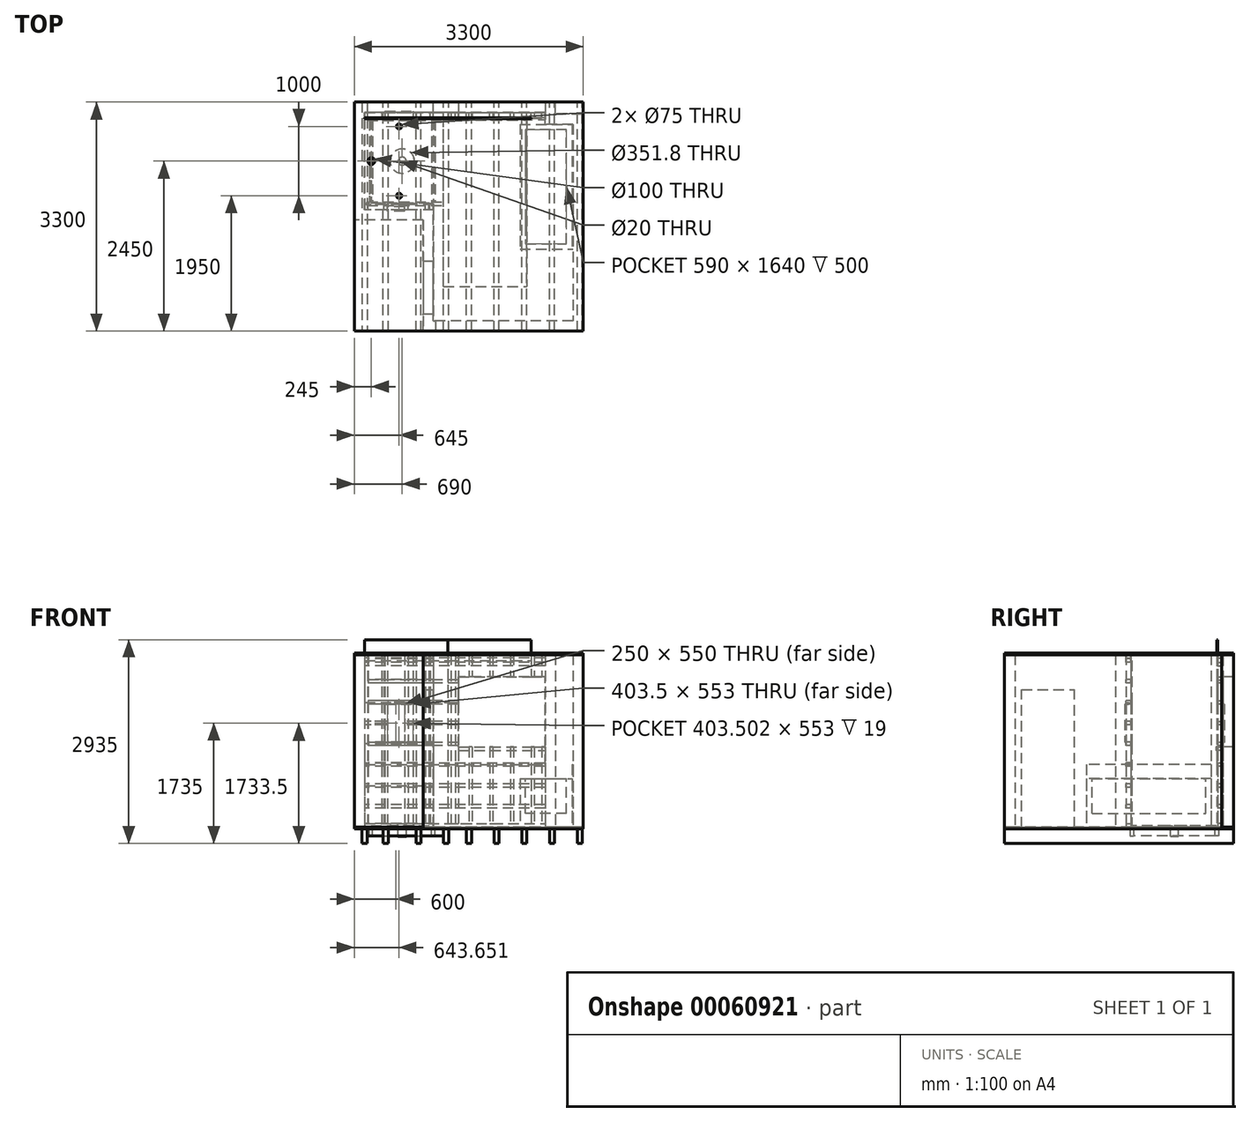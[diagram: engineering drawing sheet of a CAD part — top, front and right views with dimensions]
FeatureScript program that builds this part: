
annotation { "Feature Type Name" : "Feature", "Feature Type Description" : "" }
export const myFeature = defineFeature(function(context is Context, id is Id, definition is map)
    precondition{}
    {
        {
            var Q0;
            Q0=qCreatedBy(makeId("Top.planeOp"),FACE);
            var sketch = newSketch(context, id + "F0", { "sketchPlane" : qUnion([Q0])});
            skLineSegment(sketch, "E0.bottom", {"start": v(1500, -1500) * mm, "end": v(-510, -1500) * mm});
            skLineSegment(sketch, "E0.top", {"start": v(1100, 1500) * mm, "end": v(-1500, 1500) * mm});
            skLineSegment(sketch, "E0.left", {"start": v(1500, -1500) * mm, "end": v(1500, 1331.1) * mm});
            skLineSegment(sketch, "E0.right", {"start": v(-1500, 100) * mm, "end": v(-1500, 1500) * mm});
            skPoint(sketch, "E0.middle", {"position": v(0, 0) * mm});
            skLineSegment(sketch, "E1", {"start": v(-1500, 100) * mm, "end": v(-510, 100) * mm});
            skLineSegment(sketch, "E2", {"start": v(-510, 100) * mm, "end": v(-510, -1500) * mm});
            skLineSegment(sketch, "E3", {"start": v(1100, 1500) * mm, "end": v(1100, 1331.1) * mm});
            skLineSegment(sketch, "E4", {"start": v(1100, 1331.1) * mm, "end": v(1500, 1331.1) * mm});
            skLineSegment(sketch, "E5.0", {"start": v(1650, -1650) * mm, "end": v(1650, 1481.1) * mm});
            skLineSegment(sketch, "E5.1", {"start": v(1250, 1481.1) * mm, "end": v(1650, 1481.1) * mm});
            skLineSegment(sketch, "E5.2", {"start": v(1650, -1650) * mm, "end": v(-660, -1650) * mm});
            skLineSegment(sketch, "E5.3", {"start": v(1250, 1650) * mm, "end": v(1250, 1481.1) * mm});
            skLineSegment(sketch, "E5.4", {"start": v(-660, -50) * mm, "end": v(-660, -1650) * mm});
            skLineSegment(sketch, "E5.5", {"start": v(-1650, -50) * mm, "end": v(-660, -50) * mm});
            skLineSegment(sketch, "E5.6", {"start": v(-1650, -50) * mm, "end": v(-1650, 1650) * mm});
            skLineSegment(sketch, "E5.7", {"start": v(1250, 1650) * mm, "end": v(-1650, 1650) * mm});
            skSolve(sketch);
        }
        {
            var Q0;
            Q0=makeQuery(id+"F0.imprint","IMPRINT",FACE,{"disambiguationData":[TD([[makeQuery(id+"F0.imprint","IMPRINT",EDGE,{"derivedFrom":sQuery(id+"F0.wireOp",EDGE,"E0.bottom")}),1.0]])]});
            extrude(context, id + "F1", {"entities" : qUnion([Q0]), "depth" : 2510 * mm});
        }
        {
            var Q0;
            Q0=makeQuery(id+"F1.opExtrude","CAP_FACE",FACE,{"disambiguationData":[OSD([sQuery(id+"F0.wireOp",EDGE,"E0.bottom"),sQuery(id+"F0.wireOp",EDGE,"E0.top"),sQuery(id+"F0.wireOp",EDGE,"E0.left"),sQuery(id+"F0.wireOp",EDGE,"E0.right"),sQuery(id+"F0.wireOp",EDGE,"E1"),sQuery(id+"F0.wireOp",EDGE,"E2"),sQuery(id+"F0.wireOp",EDGE,"E3"),sQuery(id+"F0.wireOp",EDGE,"E4"),sQuery(id+"F0.wireOp",EDGE,"E5.0"),sQuery(id+"F0.wireOp",EDGE,"E5.1"),sQuery(id+"F0.wireOp",EDGE,"E5.2"),sQuery(id+"F0.wireOp",EDGE,"E5.3"),sQuery(id+"F0.wireOp",EDGE,"E5.4"),sQuery(id+"F0.wireOp",EDGE,"E5.5"),sQuery(id+"F0.wireOp",EDGE,"E5.6"),sQuery(id+"F0.wireOp",EDGE,"E5.7")])],"isStart":true});
            var sketch = newSketch(context, id + "F2", { "sketchPlane" : qUnion([Q0])});
            skLineSegment(sketch, "E6.bottom", {"start": v(1650, 1650) * mm, "end": v(-1650, 1650) * mm});
            skLineSegment(sketch, "E6.top", {"start": v(1650, -1650) * mm, "end": v(-1650, -1650) * mm});
            skLineSegment(sketch, "E6.left", {"start": v(1650, 1650) * mm, "end": v(1650, -1650) * mm});
            skLineSegment(sketch, "E6.right", {"start": v(-1650, 1650) * mm, "end": v(-1650, -1650) * mm});
            skSolve(sketch);
        }
        {
            var Q0;
            Q0 = qSketchRegion(id + "F2", true);
            extrude(context, id + "F3", {"entities" : qUnion([Q0]), "operationType" : NewBodyOperationType.ADD, "oppositeDirection" : true, "depth" : 25 * mm});
        }
        {
            var Q0;
            Q0=makeQuery(id+"F1.opExtrude","SWEPT_FACE",FACE,{"disambiguationData":[OSD([sQuery(id+"F0.wireOp",EDGE,"E2")])]});
            var sketch = newSketch(context, id + "F4", { "sketchPlane" : qUnion([Q0])});
            skLineSegment(sketch, "E7.bottom", {"start": v(-1402.14, 25) * mm, "end": v(-640.14, 25) * mm});
            skLineSegment(sketch, "E7.top", {"start": v(-1402.14, 2006) * mm, "end": v(-640.14, 2006) * mm});
            skLineSegment(sketch, "E7.left", {"start": v(-1402.14, 25) * mm, "end": v(-1402.14, 2006) * mm});
            skLineSegment(sketch, "E7.right", {"start": v(-640.14, 25) * mm, "end": v(-640.14, 2006) * mm});
            skSolve(sketch);
        }
        {
            var Q0;
            Q0 = qSketchRegion(id + "F4", true);
            extrude(context, id + "F5", {"entities" : qUnion([Q0]), "operationType" : NewBodyOperationType.REMOVE, "endBound" : BoundingType.UP_TO_NEXT, "oppositeDirection" : true, "depth" : 25 * mm});
        }
        {
            var Q0;
            Q0=makeQuery(id+"F1.opExtrude","SWEPT_FACE",FACE,{"disambiguationData":[OSD([sQuery(id+"F0.wireOp",EDGE,"E0.top")])]});
            var sketch = newSketch(context, id + "F6", { "sketchPlane" : qUnion([Q0])});
            skLineSegment(sketch, "E8.bottom", {"start": v(-150, 2190) * mm, "end": v(1100, 2190) * mm});
            skLineSegment(sketch, "E8.top", {"start": v(-150, 1180) * mm, "end": v(1100, 1180) * mm});
            skLineSegment(sketch, "E8.left", {"start": v(-150, 2190) * mm, "end": v(-150, 1180) * mm});
            skLineSegment(sketch, "E8.right", {"start": v(1100, 2190) * mm, "end": v(1100, 1180) * mm});
            skSolve(sketch);
        }
        {
            var Q0;
            Q0 = qSketchRegion(id + "F6", true);
            extrude(context, id + "F7", {"entities" : qUnion([Q0]), "operationType" : NewBodyOperationType.REMOVE, "endBound" : BoundingType.UP_TO_NEXT, "oppositeDirection" : true, "depth" : 25 * mm, "hasSecondDirection" : true, "secondDirectionBound" : BoundingType.UP_TO_NEXT, "secondDirectionOppositeDirection" : false, "secondDirectionDepth" : 25 * mm});
        }
        {
            var Q0;
            {var subQ0=sQuery(id+"F2.wireOp",EDGE,"E6.right");var subQ1=sQuery(id+"F2.wireOp",EDGE,"E6.bottom");var subQ2=makeQuery(id+"F3.opExtrude","CAP_FACE",FACE,{"disambiguationData":[OSD([subQ1,sQuery(id+"F2.wireOp",EDGE,"E6.top"),sQuery(id+"F2.wireOp",EDGE,"E6.left"),subQ0])],"isStart":false});Q0=makeQuery(id+"F5.boolean.opBoolean","MERGE",FACE,{"derivedFrom":[makeQuery(id+"F3.boolean.opBoolean","SPLIT",FACE,{"disambiguationData":[TD([makeQuery(id+"F1.opExtrude","SWEPT_FACE",FACE,{"disambiguationData":[OSD([sQuery(id+"F0.wireOp",EDGE,"E5.2")])]})])],"derivedFrom":subQ2}),makeQuery(id+"F3.boolean.opBoolean","SPLIT",FACE,{"disambiguationData":[TD([makeQuery(id+"F1.opExtrude","SWEPT_FACE",FACE,{"disambiguationData":[OSD([sQuery(id+"F0.wireOp",EDGE,"E0.bottom")])]})])],"derivedFrom":subQ2}),makeQuery(id+"F5.opExtrude","SWEPT_FACE",FACE,{"disambiguationData":[OSD([sQuery(id+"F4.wireOp",EDGE,"E7.bottom")])]})]});}
            var sketch = newSketch(context, id + "F8", { "sketchPlane" : qUnion([Q0])});
            skLineSegment(sketch, "E9.bottom", {"start": v(-1500, 1500) * mm, "end": v(1100, 1500) * mm});
            skLineSegment(sketch, "E9.top", {"start": v(-1500, 1425) * mm, "end": v(1100, 1425) * mm});
            skLineSegment(sketch, "E9.left", {"start": v(-1500, 1500) * mm, "end": v(-1500, 1425) * mm});
            skLineSegment(sketch, "E9.right", {"start": v(1100, 1500) * mm, "end": v(1100, 1425) * mm});
            skSolve(sketch);
        }
        {
            var Q0;
            Q0 = qSketchRegion(id + "F8", true);
            extrude(context, id + "F9", {"entities" : qUnion([Q0]), "depth" : 50 * mm});
        }
        {
            var Q0;
            Q0=makeQuery(id+"F9.opExtrude","CAP_FACE",FACE,{"disambiguationData":[OSD([sQuery(id+"F8.wireOp",EDGE,"E9.bottom"),sQuery(id+"F8.wireOp",EDGE,"E9.top"),sQuery(id+"F8.wireOp",EDGE,"E9.left"),sQuery(id+"F8.wireOp",EDGE,"E9.right")])],"isStart":false});
            var sketch = newSketch(context, id + "F10", { "sketchPlane" : qUnion([Q0])});
            skLineSegment(sketch, "E10.bottom", {"start": v(-1500, 1425) * mm, "end": v(-1455, 1425) * mm});
            skLineSegment(sketch, "E10.top", {"start": v(-1500, 1500) * mm, "end": v(-1455, 1500) * mm});
            skLineSegment(sketch, "E10.left", {"start": v(-1500, 1425) * mm, "end": v(-1500, 1500) * mm});
            skLineSegment(sketch, "E10.right", {"start": v(-1455, 1425) * mm, "end": v(-1455, 1500) * mm});
            skLineSegment(sketch, "E11.bottom", {"start": v(1100, 1500) * mm, "end": v(1050, 1500) * mm});
            skLineSegment(sketch, "E11.top", {"start": v(1100, 1425) * mm, "end": v(1050, 1425) * mm});
            skLineSegment(sketch, "E11.left", {"start": v(1100, 1500) * mm, "end": v(1100, 1425) * mm});
            skLineSegment(sketch, "E11.right", {"start": v(1050, 1500) * mm, "end": v(1050, 1425) * mm});
            skLineSegment(sketch, "E12.bottom", {"start": v(900, 1500) * mm, "end": v(945, 1500) * mm});
            skLineSegment(sketch, "E12.top", {"start": v(900, 1425) * mm, "end": v(945, 1425) * mm});
            skLineSegment(sketch, "E12.left", {"start": v(900, 1500) * mm, "end": v(900, 1425) * mm});
            skLineSegment(sketch, "E12.right", {"start": v(945, 1500) * mm, "end": v(945, 1425) * mm});
            skLineSegment(sketch, "E13.bottom", {"start": v(600, 1500) * mm, "end": v(645, 1500) * mm});
            skLineSegment(sketch, "E13.top", {"start": v(600, 1425) * mm, "end": v(645, 1425) * mm});
            skLineSegment(sketch, "E13.left", {"start": v(600, 1500) * mm, "end": v(600, 1425) * mm});
            skLineSegment(sketch, "E13.right", {"start": v(645, 1500) * mm, "end": v(645, 1425) * mm});
            skLineSegment(sketch, "E14.bottom", {"start": v(300, 1500) * mm, "end": v(345, 1500) * mm});
            skLineSegment(sketch, "E14.top", {"start": v(300, 1425) * mm, "end": v(345, 1425) * mm});
            skLineSegment(sketch, "E14.left", {"start": v(300, 1500) * mm, "end": v(300, 1425) * mm});
            skLineSegment(sketch, "E14.right", {"start": v(345, 1500) * mm, "end": v(345, 1425) * mm});
            skLineSegment(sketch, "E15.bottom", {"start": v(0, 1500) * mm, "end": v(45, 1500) * mm});
            skLineSegment(sketch, "E15.top", {"start": v(0, 1425) * mm, "end": v(45, 1425) * mm});
            skLineSegment(sketch, "E15.left", {"start": v(0, 1500) * mm, "end": v(0, 1425) * mm});
            skLineSegment(sketch, "E15.right", {"start": v(45, 1500) * mm, "end": v(45, 1425) * mm});
            skLineSegment(sketch, "E16.bottom", {"start": v(-300, 1500) * mm, "end": v(-255, 1500) * mm});
            skLineSegment(sketch, "E16.top", {"start": v(-300, 1425) * mm, "end": v(-255, 1425) * mm});
            skLineSegment(sketch, "E16.left", {"start": v(-300, 1500) * mm, "end": v(-300, 1425) * mm});
            skLineSegment(sketch, "E16.right", {"start": v(-255, 1500) * mm, "end": v(-255, 1425) * mm});
            skLineSegment(sketch, "E17.bottom", {"start": v(-804.6, 1500) * mm, "end": v(-757.44, 1500) * mm});
            skLineSegment(sketch, "E17.top", {"start": v(-804.6, 1425) * mm, "end": v(-757.44, 1425) * mm});
            skLineSegment(sketch, "E17.left", {"start": v(-804.6, 1500) * mm, "end": v(-804.6, 1425) * mm});
            skLineSegment(sketch, "E17.right", {"start": v(-757.44, 1500) * mm, "end": v(-757.44, 1425) * mm});
            skLineSegment(sketch, "E18.bottom", {"start": v(-1255.25, 1500) * mm, "end": v(-1208.1, 1500) * mm});
            skLineSegment(sketch, "E18.top", {"start": v(-1255.25, 1425) * mm, "end": v(-1208.1, 1425) * mm});
            skLineSegment(sketch, "E18.left", {"start": v(-1255.25, 1500) * mm, "end": v(-1255.25, 1425) * mm});
            skLineSegment(sketch, "E18.right", {"start": v(-1208.1, 1500) * mm, "end": v(-1208.1, 1425) * mm});
            skLineSegment(sketch, "E19.bottom", {"start": v(-195, 1425) * mm, "end": v(-150, 1425) * mm});
            skLineSegment(sketch, "E19.top", {"start": v(-195, 1500) * mm, "end": v(-150, 1500) * mm});
            skLineSegment(sketch, "E19.left", {"start": v(-195, 1425) * mm, "end": v(-195, 1500) * mm});
            skLineSegment(sketch, "E19.right", {"start": v(-150, 1425) * mm, "end": v(-150, 1500) * mm});
            skLineSegment(sketch, "E20.bottom", {"start": v(-555, 1425) * mm, "end": v(-510, 1425) * mm});
            skLineSegment(sketch, "E20.top", {"start": v(-555, 1500) * mm, "end": v(-510, 1500) * mm});
            skLineSegment(sketch, "E20.left", {"start": v(-555, 1425) * mm, "end": v(-555, 1500) * mm});
            skLineSegment(sketch, "E20.right", {"start": v(-510, 1425) * mm, "end": v(-510, 1500) * mm});
            skSolve(sketch);
        }
        {
            var Q0;
            Q0 = qSketchRegion(id + "F10", true);
            var Q1;
            Q1=makeQuery(id+"F1.opExtrude","CAP_FACE",FACE,{"disambiguationData":[OSD([sQuery(id+"F0.wireOp",EDGE,"E0.bottom"),sQuery(id+"F0.wireOp",EDGE,"E0.top"),sQuery(id+"F0.wireOp",EDGE,"E0.left"),sQuery(id+"F0.wireOp",EDGE,"E0.right"),sQuery(id+"F0.wireOp",EDGE,"E1"),sQuery(id+"F0.wireOp",EDGE,"E2"),sQuery(id+"F0.wireOp",EDGE,"E3"),sQuery(id+"F0.wireOp",EDGE,"E4"),sQuery(id+"F0.wireOp",EDGE,"E5.0"),sQuery(id+"F0.wireOp",EDGE,"E5.1"),sQuery(id+"F0.wireOp",EDGE,"E5.2"),sQuery(id+"F0.wireOp",EDGE,"E5.3"),sQuery(id+"F0.wireOp",EDGE,"E5.4"),sQuery(id+"F0.wireOp",EDGE,"E5.5"),sQuery(id+"F0.wireOp",EDGE,"E5.6"),sQuery(id+"F0.wireOp",EDGE,"E5.7")])],"isStart":false});
            extrude(context, id + "F11", {"entities" : qUnion([Q0]), "endBound" : BoundingType.UP_TO_SURFACE, "endBoundEntityFace" : qUnion([Q1]), "depth" : 25 * mm});
        }
        {
            var Q0;
            Q0=makeQuery(id+"F1.opExtrude","SWEPT_FACE",FACE,{"disambiguationData":[OSD([sQuery(id+"F0.wireOp",EDGE,"E0.right")])]});
            var sketch = newSketch(context, id + "F12", { "sketchPlane" : qUnion([Q0])});
            skLineSegment(sketch, "E21.bottom", {"start": v(1425, 2510) * mm, "end": v(1500, 2510) * mm});
            skLineSegment(sketch, "E21.top", {"start": v(1425, 2463) * mm, "end": v(1500, 2463) * mm});
            skLineSegment(sketch, "E21.left", {"start": v(1425, 2510) * mm, "end": v(1425, 2463) * mm});
            skLineSegment(sketch, "E21.right", {"start": v(1500, 2510) * mm, "end": v(1500, 2463) * mm});
            skLineSegment(sketch, "E22.bottom", {"start": v(1500, 2147) * mm, "end": v(1425, 2147) * mm});
            skLineSegment(sketch, "E22.top", {"start": v(1500, 2100) * mm, "end": v(1425, 2100) * mm});
            skLineSegment(sketch, "E22.left", {"start": v(1500, 2147) * mm, "end": v(1500, 2100) * mm});
            skLineSegment(sketch, "E22.right", {"start": v(1425, 2147) * mm, "end": v(1425, 2100) * mm});
            skLineSegment(sketch, "E23.bottom", {"start": v(1500, 1847) * mm, "end": v(1425, 1847) * mm});
            skLineSegment(sketch, "E23.top", {"start": v(1500, 1800) * mm, "end": v(1425, 1800) * mm});
            skLineSegment(sketch, "E23.left", {"start": v(1500, 1847) * mm, "end": v(1500, 1800) * mm});
            skLineSegment(sketch, "E23.right", {"start": v(1425, 1847) * mm, "end": v(1425, 1800) * mm});
            skLineSegment(sketch, "E24.bottom", {"start": v(1500, 1547) * mm, "end": v(1425, 1547) * mm});
            skLineSegment(sketch, "E24.top", {"start": v(1500, 1500) * mm, "end": v(1425, 1500) * mm});
            skLineSegment(sketch, "E24.left", {"start": v(1500, 1547) * mm, "end": v(1500, 1500) * mm});
            skLineSegment(sketch, "E24.right", {"start": v(1425, 1547) * mm, "end": v(1425, 1500) * mm});
            skLineSegment(sketch, "E25.bottom", {"start": v(1500, 1247) * mm, "end": v(1425, 1247) * mm});
            skLineSegment(sketch, "E25.top", {"start": v(1500, 1200) * mm, "end": v(1425, 1200) * mm});
            skLineSegment(sketch, "E25.left", {"start": v(1500, 1247) * mm, "end": v(1500, 1200) * mm});
            skLineSegment(sketch, "E25.right", {"start": v(1425, 1247) * mm, "end": v(1425, 1200) * mm});
            skLineSegment(sketch, "E26.bottom", {"start": v(1500, 947) * mm, "end": v(1425, 947) * mm});
            skLineSegment(sketch, "E26.top", {"start": v(1500, 900) * mm, "end": v(1425, 900) * mm});
            skLineSegment(sketch, "E26.left", {"start": v(1500, 947) * mm, "end": v(1500, 900) * mm});
            skLineSegment(sketch, "E26.right", {"start": v(1425, 947) * mm, "end": v(1425, 900) * mm});
            skLineSegment(sketch, "E27.bottom", {"start": v(1500, 647) * mm, "end": v(1425, 647) * mm});
            skLineSegment(sketch, "E27.top", {"start": v(1500, 600) * mm, "end": v(1425, 600) * mm});
            skLineSegment(sketch, "E27.left", {"start": v(1500, 647) * mm, "end": v(1500, 600) * mm});
            skLineSegment(sketch, "E27.right", {"start": v(1425, 647) * mm, "end": v(1425, 600) * mm});
            skLineSegment(sketch, "E28.bottom", {"start": v(1500, 347) * mm, "end": v(1425, 347) * mm});
            skLineSegment(sketch, "E28.top", {"start": v(1500, 300) * mm, "end": v(1425, 300) * mm});
            skLineSegment(sketch, "E28.left", {"start": v(1500, 347) * mm, "end": v(1500, 300) * mm});
            skLineSegment(sketch, "E28.right", {"start": v(1425, 347) * mm, "end": v(1425, 300) * mm});
            skLineSegment(sketch, "E29.bottom", {"start": v(1425, 2400) * mm, "end": v(1500, 2400) * mm});
            skLineSegment(sketch, "E29.top", {"start": v(1425, 2353) * mm, "end": v(1500, 2353) * mm});
            skLineSegment(sketch, "E29.left", {"start": v(1425, 2400) * mm, "end": v(1425, 2353) * mm});
            skLineSegment(sketch, "E29.right", {"start": v(1500, 2400) * mm, "end": v(1500, 2353) * mm});
            skSolve(sketch);
        }
        {
            var Q0;
            Q0 = qSketchRegion(id + "F12", true);
            var Q1;
            Q1=makeQuery(id+"F7.boolean.opBoolean","MERGE",FACE,{"derivedFrom":[makeQuery(id+"F1.opExtrude","SWEPT_FACE",FACE,{"disambiguationData":[OSD([sQuery(id+"F0.wireOp",EDGE,"E3")])]}),makeQuery(id+"F7.opExtrude","SWEPT_FACE",FACE,{"disambiguationData":[OSD([sQuery(id+"F6.wireOp",EDGE,"E8.right")])]})]});
            extrude(context, id + "F13", {"entities" : qUnion([Q0]), "endBound" : BoundingType.UP_TO_SURFACE, "endBoundEntityFace" : qUnion([Q1]), "depth" : 25 * mm});
        }
        {
            var Q0;
            Q0=makeQuery(id+"F11.opExtrude","SWEPT_FACE",FACE,{"disambiguationData":[OSD([sQuery(id+"F10.wireOp",EDGE,"E17.top")])]});
            var sketch = newSketch(context, id + "F14", { "sketchPlane" : qUnion([Q0])});
            skLineSegment(sketch, "E30.bottom", {"start": v(-1500, 925) * mm, "end": v(-300, 925) * mm});
            skLineSegment(sketch, "E30.top", {"start": v(-1500, 25) * mm, "end": v(-300, 25) * mm});
            skLineSegment(sketch, "E30.left", {"start": v(-1500, 925) * mm, "end": v(-1500, 25) * mm});
            skLineSegment(sketch, "E30.right", {"start": v(-300, 925) * mm, "end": v(-300, 25) * mm});
            skSolve(sketch);
        }
        {
            var Q0;
            Q0 = qSketchRegion(id + "F14", true);
            extrude(context, id + "F15", {"entities" : qUnion([Q0]), "depth" : 12 * mm});
        }
        {
            var Q0;
            Q0=makeQuery(id+"F15.opExtrude","SWEPT_BODY",BODY,{"disambiguationData":[OSD([sQuery(id+"F14.wireOp",EDGE,"E30.bottom"),sQuery(id+"F14.wireOp",EDGE,"E30.top"),sQuery(id+"F14.wireOp",EDGE,"E30.left"),sQuery(id+"F14.wireOp",EDGE,"E30.right")])]});
            transform(context, id + "F16", {"entities" : qUnion([Q0]), "transformType" : TransformType.COPY});
        }
        {
            var Q0;
            Q0=makeQuery(id+"F15.opExtrude","SWEPT_BODY",BODY,{"disambiguationData":[OSD([sQuery(id+"F14.wireOp",EDGE,"E30.bottom"),sQuery(id+"F14.wireOp",EDGE,"E30.top"),sQuery(id+"F14.wireOp",EDGE,"E30.left"),sQuery(id+"F14.wireOp",EDGE,"E30.right")])]});
            transform(context, id + "F17", {"entities" : qUnion([Q0]), "transformType" : TransformType.TRANSLATION_3D, "dx" : 0 * mm, "dy" : 0 * mm, "dz" : 900 * mm, "makeCopy" : true});
        }
        {
            var Q0;
            Q0=makeQuery(id+"F17.opPattern","COPY",BODY,{"derivedFrom":makeQuery(id+"F15.opExtrude","SWEPT_BODY",BODY,{"disambiguationData":[OSD([sQuery(id+"F14.wireOp",EDGE,"E30.bottom"),sQuery(id+"F14.wireOp",EDGE,"E30.top"),sQuery(id+"F14.wireOp",EDGE,"E30.left"),sQuery(id+"F14.wireOp",EDGE,"E30.right")])]}),"instanceName":"1"});
            transform(context, id + "F18", {"entities" : qUnion([Q0]), "transformType" : TransformType.TRANSLATION_3D, "dx" : 0 * mm, "dy" : 0 * mm, "dz" : 900 * mm, "makeCopy" : true});
        }
        {
            var Q0;
            Q0=makeQuery(id+"F18.opPattern","COPY",BODY,{"derivedFrom":makeQuery(id+"F17.opPattern","COPY",BODY,{"derivedFrom":makeQuery(id+"F15.opExtrude","SWEPT_BODY",BODY,{"disambiguationData":[OSD([sQuery(id+"F14.wireOp",EDGE,"E30.bottom"),sQuery(id+"F14.wireOp",EDGE,"E30.top"),sQuery(id+"F14.wireOp",EDGE,"E30.left"),sQuery(id+"F14.wireOp",EDGE,"E30.right")])]}),"instanceName":"1"}),"instanceName":"1"});
            transform(context, id + "F19", {"entities" : qUnion([Q0]), "transformType" : TransformType.TRANSLATION_3D, "dx" : 1200 * mm, "dy" : 0 * mm, "dz" : 0 * mm, "makeCopy" : true});
        }
        {
            var Q0;
            Q0=makeQuery(id+"F17.opPattern","COPY",BODY,{"derivedFrom":makeQuery(id+"F15.opExtrude","SWEPT_BODY",BODY,{"disambiguationData":[OSD([sQuery(id+"F14.wireOp",EDGE,"E30.bottom"),sQuery(id+"F14.wireOp",EDGE,"E30.top"),sQuery(id+"F14.wireOp",EDGE,"E30.left"),sQuery(id+"F14.wireOp",EDGE,"E30.right")])]}),"instanceName":"1"});
            transform(context, id + "F20", {"entities" : qUnion([Q0]), "transformType" : TransformType.TRANSLATION_3D, "dx" : 1200 * mm, "dy" : 0 * mm, "dz" : 0 * mm, "makeCopy" : true});
        }
        {
            var Q0;
            Q0=makeQuery(id+"F15.opExtrude","SWEPT_BODY",BODY,{"disambiguationData":[OSD([sQuery(id+"F14.wireOp",EDGE,"E30.bottom"),sQuery(id+"F14.wireOp",EDGE,"E30.top"),sQuery(id+"F14.wireOp",EDGE,"E30.left"),sQuery(id+"F14.wireOp",EDGE,"E30.right")])]});
            transform(context, id + "F21", {"entities" : qUnion([Q0]), "transformType" : TransformType.TRANSLATION_3D, "dx" : 1200 * mm, "dy" : 0 * mm, "dz" : 0 * mm, "makeCopy" : true});
        }
        {
            var Q0;
            Q0=makeQuery(id+"F3.boolean.opBoolean","MERGE",FACE,{"derivedFrom":[makeQuery(id+"F1.opExtrude","SWEPT_FACE",FACE,{"disambiguationData":[OSD([sQuery(id+"F0.wireOp",EDGE,"E5.7")])]}),makeQuery(id+"F3.opExtrude","SWEPT_FACE",FACE,{"disambiguationData":[OSD([sQuery(id+"F2.wireOp",EDGE,"E6.top")])]})]});
            var sketch = newSketch(context, id + "F22", { "sketchPlane" : qUnion([Q0])});
            skLineSegment(sketch, "E31.bottom", {"start": v(-1100, 2190) * mm, "end": v(150, 2190) * mm});
            skLineSegment(sketch, "E31.top", {"start": v(-1100, 1180) * mm, "end": v(150, 1180) * mm});
            skLineSegment(sketch, "E31.left", {"start": v(-1100, 2190) * mm, "end": v(-1100, 1180) * mm});
            skLineSegment(sketch, "E31.right", {"start": v(150, 2190) * mm, "end": v(150, 1180) * mm});
            skSolve(sketch);
        }
        {
            var Q0;
            Q0=makeQuery(id+"F7.boolean.opBoolean","MERGE",FACE,{"derivedFrom":[makeQuery(id+"F1.opExtrude","SWEPT_FACE",FACE,{"disambiguationData":[OSD([sQuery(id+"F0.wireOp",EDGE,"E3")])]}),makeQuery(id+"F7.opExtrude","SWEPT_FACE",FACE,{"disambiguationData":[OSD([sQuery(id+"F6.wireOp",EDGE,"E8.right")])]})]});
            var sketch = newSketch(context, id + "F23", { "sketchPlane" : qUnion([Q0])});
            skLineSegment(sketch, "E32.bottom", {"start": v(-1500, 1180) * mm, "end": v(-1400, 1180) * mm});
            skLineSegment(sketch, "E32.top", {"start": v(-1500, 1130) * mm, "end": v(-1400, 1130) * mm});
            skLineSegment(sketch, "E32.left", {"start": v(-1500, 1180) * mm, "end": v(-1500, 1130) * mm});
            skLineSegment(sketch, "E32.right", {"start": v(-1400, 1180) * mm, "end": v(-1400, 1130) * mm});
            skSolve(sketch);
        }
        {
            var Q0;
            Q0 = qSketchRegion(id + "F23", true);
            var Q1;
            Q1=makeQuery(id+"F11.opExtrude","SWEPT_FACE",FACE,{"disambiguationData":[OSD([sQuery(id+"F10.wireOp",EDGE,"E19.right")])]});
            extrude(context, id + "F24", {"entities" : qUnion([Q0]), "endBound" : BoundingType.UP_TO_SURFACE, "endBoundEntityFace" : qUnion([Q1]), "depth" : 25 * mm});
        }
        {
            var Q0;
            Q0=makeQuery(id+"F13.opExtrude","SWEPT_FACE",FACE,{"disambiguationData":[OSD([sQuery(id+"F12.wireOp",EDGE,"E21.left")])]});
            var sketch = newSketch(context, id + "F25", { "sketchPlane" : qUnion([Q0])});
            skLineSegment(sketch, "E33.bottom", {"start": v(-1500, 2510) * mm, "end": v(-300, 2510) * mm});
            skLineSegment(sketch, "E33.top", {"start": v(-1500, 2425) * mm, "end": v(-300, 2425) * mm});
            skLineSegment(sketch, "E33.left", {"start": v(-1500, 2510) * mm, "end": v(-1500, 2425) * mm});
            skLineSegment(sketch, "E33.right", {"start": v(-300, 2510) * mm, "end": v(-300, 2425) * mm});
            skSolve(sketch);
        }
        {
            var Q0;
            Q0 = qSketchRegion(id + "F25", true);
            extrude(context, id + "F26", {"entities" : qUnion([Q0]), "depth" : 6 * mm});
        }
        {
            var Q0;
            Q0=makeQuery(id+"F13.opExtrude","SWEPT_FACE",FACE,{"disambiguationData":[OSD([sQuery(id+"F12.wireOp",EDGE,"E21.left")])]});
            var sketch = newSketch(context, id + "F27", { "sketchPlane" : qUnion([Q0])});
            skLineSegment(sketch, "E34.bottom", {"start": v(-300, 2510) * mm, "end": v(900, 2510) * mm});
            skLineSegment(sketch, "E34.top", {"start": v(-300, 2425) * mm, "end": v(900, 2425) * mm});
            skLineSegment(sketch, "E34.left", {"start": v(-300, 2510) * mm, "end": v(-300, 2425) * mm});
            skLineSegment(sketch, "E34.right", {"start": v(900, 2510) * mm, "end": v(900, 2425) * mm});
            skSolve(sketch);
        }
        {
            var Q0;
            Q0 = qSketchRegion(id + "F27", true);
            extrude(context, id + "F28", {"entities" : qUnion([Q0]), "depth" : 6 * mm});
        }
        {
            var Q0;
            Q0=makeQuery(id+"F7.boolean.opBoolean","COPY",FACE,{"derivedFrom":makeQuery(id+"F7.opExtrude","SWEPT_FACE",FACE,{"disambiguationData":[OSD([sQuery(id+"F6.wireOp",EDGE,"E8.left")])]})});
            var sketch = newSketch(context, id + "F29", { "sketchPlane" : qUnion([Q0])});
            skLineSegment(sketch, "E35.bottom", {"start": v(1500, 2190) * mm, "end": v(1394, 2190) * mm});
            skLineSegment(sketch, "E35.top", {"start": v(1500, 1180) * mm, "end": v(1394, 1180) * mm});
            skLineSegment(sketch, "E35.left", {"start": v(1500, 2190) * mm, "end": v(1500, 1180) * mm});
            skLineSegment(sketch, "E35.right", {"start": v(1394, 2190) * mm, "end": v(1394, 1180) * mm});
            skSolve(sketch);
        }
        {
            var Q0;
            Q0 = qSketchRegion(id + "F29", true);
            extrude(context, id + "F30", {"entities" : qUnion([Q0]), "depth" : 6 * mm});
        }
        {
            var Q0;
            Q0=makeQuery(id+"F24.opExtrude","SWEPT_FACE",FACE,{"disambiguationData":[OSD([sQuery(id+"F23.wireOp",EDGE,"E32.bottom")])]});
            var sketch = newSketch(context, id + "F31", { "sketchPlane" : qUnion([Q0])});
            skLineSegment(sketch, "E36.bottom", {"start": v(-144.51, 1500) * mm, "end": v(1099.49, 1506) * mm});
            skLineSegment(sketch, "E36.top", {"start": v(-144, 1394) * mm, "end": v(1100, 1400) * mm});
            skLineSegment(sketch, "E36.left", {"start": v(-144.51, 1500) * mm, "end": v(-144, 1394) * mm});
            skLineSegment(sketch, "E36.right", {"start": v(1099.49, 1506) * mm, "end": v(1100, 1400) * mm});
            skSolve(sketch);
        }
        {
            var Q0;
            Q0 = qSketchRegion(id + "F31", true);
            extrude(context, id + "F32", {"entities" : qUnion([Q0]), "depth" : 6 * mm});
        }
        {
            var Q0;
            {var subQ2=sQuery(id+"F10.wireOp",EDGE,"E12.top");Q0=makeQuery(id+"F35.boolean.opBoolean","SPLIT",FACE,{"disambiguationData":[TD([makeQuery(id+"F35.opExtrude","SWEPT_FACE",FACE,{"disambiguationData":[OSD([sQuery(id+"F22.wireOp",EDGE,"E31.top")])]})])],"derivedFrom":makeQuery(id+"F11.opExtrude","SWEPT_FACE",FACE,{"disambiguationData":[OSD([subQ2])]})});}
            var sketch = newSketch(context, id + "F33", { "sketchPlane" : qUnion([Q0])});
            skLineSegment(sketch, "E37.bottom", {"start": v(900, 925) * mm, "end": v(1100, 925) * mm});
            skLineSegment(sketch, "E37.top", {"start": v(900, 1525) * mm, "end": v(1100, 1525) * mm});
            skLineSegment(sketch, "E37.left", {"start": v(900, 925) * mm, "end": v(900, 1525) * mm});
            skLineSegment(sketch, "E37.right", {"start": v(1100, 925) * mm, "end": v(1100, 1525) * mm});
            skSolve(sketch);
        }
        {
            var Q0;
            Q0 = qSketchRegion(id + "F33", true);
            extrude(context, id + "F34", {"entities" : qUnion([Q0]), "depth" : 6 * mm});
        }
        {
            var Q0;
            Q0 = qSketchRegion(id + "F22", true);
            extrude(context, id + "F35", {"entities" : qUnion([Q0]), "operationType" : NewBodyOperationType.REMOVE, "oppositeDirection" : true, "depth" : 350 * mm});
        }
        {
            var Q0;
            {var subQ2=sQuery(id+"F10.wireOp",EDGE,"E11.top");Q0=makeQuery(id+"F35.boolean.opBoolean","SPLIT",FACE,{"disambiguationData":[TD([makeQuery(id+"F35.opExtrude","SWEPT_FACE",FACE,{"disambiguationData":[OSD([sQuery(id+"F22.wireOp",EDGE,"E31.top")])]})])],"derivedFrom":makeQuery(id+"F11.opExtrude","SWEPT_FACE",FACE,{"disambiguationData":[OSD([subQ2])]})});}
            var sketch = newSketch(context, id + "F36", { "sketchPlane" : qUnion([Q0])});
            skLineSegment(sketch, "E38.bottom", {"start": v(900, 925) * mm, "end": v(1100, 925) * mm});
            skLineSegment(sketch, "E38.top", {"start": v(900, 25) * mm, "end": v(1100, 25) * mm});
            skLineSegment(sketch, "E38.left", {"start": v(900, 925) * mm, "end": v(900, 25) * mm});
            skLineSegment(sketch, "E38.right", {"start": v(1100, 925) * mm, "end": v(1100, 25) * mm});
            skSolve(sketch);
        }
        {
            var Q0;
            Q0 = qSketchRegion(id + "F36", true);
            extrude(context, id + "F37", {"entities" : qUnion([Q0]), "depth" : 6 * mm});
        }
        {
            var Q0;
            Q0=makeQuery(id+"F13.opExtrude","SWEPT_FACE",FACE,{"disambiguationData":[OSD([sQuery(id+"F12.wireOp",EDGE,"E21.left")])]});
            var sketch = newSketch(context, id + "F38", { "sketchPlane" : qUnion([Q0])});
            skLineSegment(sketch, "E39.bottom", {"start": v(900, 2510) * mm, "end": v(1100, 2510) * mm});
            skLineSegment(sketch, "E39.top", {"start": v(900, 2190) * mm, "end": v(1100, 2190) * mm});
            skLineSegment(sketch, "E39.left", {"start": v(900, 2510) * mm, "end": v(900, 2190) * mm});
            skLineSegment(sketch, "E39.right", {"start": v(1100, 2510) * mm, "end": v(1100, 2190) * mm});
            skSolve(sketch);
        }
        {
            var Q0;
            Q0 = qSketchRegion(id + "F38", true);
            extrude(context, id + "F39", {"entities" : qUnion([Q0]), "depth" : 6 * mm});
        }
        {
            var Q0;
            Q0=makeQuery(id+"F18.opPattern","COPY",FACE,{"derivedFrom":makeQuery(id+"F17.opPattern","COPY",FACE,{"derivedFrom":makeQuery(id+"F15.opExtrude","CAP_FACE",FACE,{"disambiguationData":[OSD([sQuery(id+"F14.wireOp",EDGE,"E30.bottom"),sQuery(id+"F14.wireOp",EDGE,"E30.top"),sQuery(id+"F14.wireOp",EDGE,"E30.left"),sQuery(id+"F14.wireOp",EDGE,"E30.right")])],"isStart":false}),"instanceName":"1"}),"instanceName":"1"});
            var sketch = newSketch(context, id + "F40", { "sketchPlane" : qUnion([Q0])});
            skLineSegment(sketch, "E40.bottom", {"start": v(-1208.1, 1800) * mm, "end": v(-804.6, 1800) * mm});
            skLineSegment(sketch, "E40.top", {"start": v(-1208.1, 1247) * mm, "end": v(-804.6, 1247) * mm});
            skLineSegment(sketch, "E40.left", {"start": v(-1208.1, 1800) * mm, "end": v(-1208.1, 1247) * mm});
            skLineSegment(sketch, "E40.right", {"start": v(-804.6, 1800) * mm, "end": v(-804.6, 1247) * mm});
            skSolve(sketch);
        }
        {
            var Q0;
            Q0 = qSketchRegion(id + "F40", true);
            extrude(context, id + "F41", {"entities" : qUnion([Q0]), "operationType" : NewBodyOperationType.REMOVE, "oppositeDirection" : true, "depth" : 106 * mm});
        }
        {
            var Q0;
            {var subQ0=sQuery(id+"F2.wireOp",EDGE,"E6.right");var subQ1=sQuery(id+"F2.wireOp",EDGE,"E6.bottom");var subQ2=makeQuery(id+"F3.opExtrude","CAP_FACE",FACE,{"disambiguationData":[OSD([subQ1,sQuery(id+"F2.wireOp",EDGE,"E6.top"),sQuery(id+"F2.wireOp",EDGE,"E6.left"),subQ0])],"isStart":false});Q0=makeQuery(id+"F5.boolean.opBoolean","MERGE",FACE,{"derivedFrom":[makeQuery(id+"F3.boolean.opBoolean","SPLIT",FACE,{"disambiguationData":[TD([makeQuery(id+"F1.opExtrude","SWEPT_FACE",FACE,{"disambiguationData":[OSD([sQuery(id+"F0.wireOp",EDGE,"E5.2")])]})])],"derivedFrom":subQ2}),makeQuery(id+"F3.boolean.opBoolean","SPLIT",FACE,{"disambiguationData":[TD([makeQuery(id+"F1.opExtrude","SWEPT_FACE",FACE,{"disambiguationData":[OSD([sQuery(id+"F0.wireOp",EDGE,"E0.bottom")])]})])],"derivedFrom":subQ2}),makeQuery(id+"F5.opExtrude","SWEPT_FACE",FACE,{"disambiguationData":[OSD([sQuery(id+"F4.wireOp",EDGE,"E7.bottom")])]})]});}
            var sketch = newSketch(context, id + "F42", { "sketchPlane" : qUnion([Q0])});
            skLineSegment(sketch, "E41.bottom", {"start": v(-510, 100) * mm, "end": v(-1500, 100) * mm});
            skLineSegment(sketch, "E41.top", {"start": v(-510, 175) * mm, "end": v(-1500, 175) * mm});
            skLineSegment(sketch, "E41.left", {"start": v(-510, 100) * mm, "end": v(-510, 175) * mm});
            skLineSegment(sketch, "E41.right", {"start": v(-1500, 100) * mm, "end": v(-1500, 175) * mm});
            skSolve(sketch);
        }
        {
            var Q0;
            Q0 = qSketchRegion(id + "F42", true);
            extrude(context, id + "F43", {"entities" : qUnion([Q0]), "depth" : 50 * mm});
        }
        {
            var Q0;
            Q0=makeQuery(id+"F43.opExtrude","CAP_FACE",FACE,{"disambiguationData":[OSD([sQuery(id+"F42.wireOp",EDGE,"E41.bottom"),sQuery(id+"F42.wireOp",EDGE,"E41.top"),sQuery(id+"F42.wireOp",EDGE,"E41.left"),sQuery(id+"F42.wireOp",EDGE,"E41.right")])],"isStart":false});
            var sketch = newSketch(context, id + "F44", { "sketchPlane" : qUnion([Q0])});
            skLineSegment(sketch, "E42.bottom", {"start": v(-510, 100) * mm, "end": v(-560, 100) * mm});
            skLineSegment(sketch, "E42.top", {"start": v(-510, 175) * mm, "end": v(-560, 175) * mm});
            skLineSegment(sketch, "E42.left", {"start": v(-510, 100) * mm, "end": v(-510, 175) * mm});
            skLineSegment(sketch, "E42.right", {"start": v(-560, 100) * mm, "end": v(-560, 175) * mm});
            skLineSegment(sketch, "E43.bottom", {"start": v(-1500, 100) * mm, "end": v(-1450, 100) * mm});
            skLineSegment(sketch, "E43.top", {"start": v(-1500, 175) * mm, "end": v(-1450, 175) * mm});
            skLineSegment(sketch, "E43.left", {"start": v(-1500, 100) * mm, "end": v(-1500, 175) * mm});
            skLineSegment(sketch, "E43.right", {"start": v(-1450, 100) * mm, "end": v(-1450, 175) * mm});
            skLineSegment(sketch, "E44.bottom", {"start": v(-1175, 100) * mm, "end": v(-1225, 100) * mm});
            skLineSegment(sketch, "E44.top", {"start": v(-1175, 175) * mm, "end": v(-1225, 175) * mm});
            skLineSegment(sketch, "E44.left", {"start": v(-1175, 100) * mm, "end": v(-1175, 175) * mm});
            skLineSegment(sketch, "E44.right", {"start": v(-1225, 100) * mm, "end": v(-1225, 175) * mm});
            skLineSegment(sketch, "E45.bottom", {"start": v(-875, 100) * mm, "end": v(-925, 100) * mm});
            skLineSegment(sketch, "E45.top", {"start": v(-875, 175) * mm, "end": v(-925, 175) * mm});
            skLineSegment(sketch, "E45.left", {"start": v(-875, 100) * mm, "end": v(-875, 175) * mm});
            skLineSegment(sketch, "E45.right", {"start": v(-925, 100) * mm, "end": v(-925, 175) * mm});
            skLineSegment(sketch, "E46.bottom", {"start": v(-625, 100) * mm, "end": v(-575, 100) * mm});
            skLineSegment(sketch, "E46.top", {"start": v(-625, 175) * mm, "end": v(-575, 175) * mm});
            skLineSegment(sketch, "E46.left", {"start": v(-625, 100) * mm, "end": v(-625, 175) * mm});
            skLineSegment(sketch, "E46.right", {"start": v(-575, 100) * mm, "end": v(-575, 175) * mm});
            skSolve(sketch);
        }
        {
            var Q0;
            Q0 = qSketchRegion(id + "F44", true);
            var Q1;
            Q1=makeQuery(id+"F1.opExtrude","CAP_FACE",FACE,{"disambiguationData":[OSD([sQuery(id+"F0.wireOp",EDGE,"E0.bottom"),sQuery(id+"F0.wireOp",EDGE,"E0.top"),sQuery(id+"F0.wireOp",EDGE,"E0.left"),sQuery(id+"F0.wireOp",EDGE,"E0.right"),sQuery(id+"F0.wireOp",EDGE,"E1"),sQuery(id+"F0.wireOp",EDGE,"E2"),sQuery(id+"F0.wireOp",EDGE,"E3"),sQuery(id+"F0.wireOp",EDGE,"E4"),sQuery(id+"F0.wireOp",EDGE,"E5.0"),sQuery(id+"F0.wireOp",EDGE,"E5.1"),sQuery(id+"F0.wireOp",EDGE,"E5.2"),sQuery(id+"F0.wireOp",EDGE,"E5.3"),sQuery(id+"F0.wireOp",EDGE,"E5.4"),sQuery(id+"F0.wireOp",EDGE,"E5.5"),sQuery(id+"F0.wireOp",EDGE,"E5.6"),sQuery(id+"F0.wireOp",EDGE,"E5.7")])],"isStart":false});
            extrude(context, id + "F45", {"entities" : qUnion([Q0]), "endBound" : BoundingType.UP_TO_SURFACE, "endBoundEntityFace" : qUnion([Q1]), "depth" : 25 * mm});
        }
        {
            var Q0;
            Q0=makeQuery(id+"F45.opExtrude","SWEPT_FACE",FACE,{"disambiguationData":[OSD([sQuery(id+"F44.wireOp",EDGE,"E43.right")])]});
            var sketch = newSketch(context, id + "F46", { "sketchPlane" : qUnion([Q0])});
            skLineSegment(sketch, "E47.bottom", {"start": v(100, 350) * mm, "end": v(175, 350) * mm});
            skLineSegment(sketch, "E47.top", {"start": v(100, 300) * mm, "end": v(175, 300) * mm});
            skLineSegment(sketch, "E47.left", {"start": v(100, 350) * mm, "end": v(100, 300) * mm});
            skLineSegment(sketch, "E47.right", {"start": v(175, 350) * mm, "end": v(175, 300) * mm});
            skLineSegment(sketch, "E48.bottom", {"start": v(100, 650) * mm, "end": v(175, 650) * mm});
            skLineSegment(sketch, "E48.top", {"start": v(100, 600) * mm, "end": v(175, 600) * mm});
            skLineSegment(sketch, "E48.left", {"start": v(100, 650) * mm, "end": v(100, 600) * mm});
            skLineSegment(sketch, "E48.right", {"start": v(175, 650) * mm, "end": v(175, 600) * mm});
            skLineSegment(sketch, "E49.bottom", {"start": v(100, 950) * mm, "end": v(175, 950) * mm});
            skLineSegment(sketch, "E49.top", {"start": v(100, 900) * mm, "end": v(175, 900) * mm});
            skLineSegment(sketch, "E49.left", {"start": v(100, 950) * mm, "end": v(100, 900) * mm});
            skLineSegment(sketch, "E49.right", {"start": v(175, 950) * mm, "end": v(175, 900) * mm});
            skLineSegment(sketch, "E50.bottom", {"start": v(100, 1250) * mm, "end": v(175, 1250) * mm});
            skLineSegment(sketch, "E50.top", {"start": v(100, 1200) * mm, "end": v(175, 1200) * mm});
            skLineSegment(sketch, "E50.left", {"start": v(100, 1250) * mm, "end": v(100, 1200) * mm});
            skLineSegment(sketch, "E50.right", {"start": v(175, 1250) * mm, "end": v(175, 1200) * mm});
            skLineSegment(sketch, "E51.bottom", {"start": v(100, 1550) * mm, "end": v(175, 1550) * mm});
            skLineSegment(sketch, "E51.top", {"start": v(100, 1500) * mm, "end": v(175, 1500) * mm});
            skLineSegment(sketch, "E51.left", {"start": v(100, 1550) * mm, "end": v(100, 1500) * mm});
            skLineSegment(sketch, "E51.right", {"start": v(175, 1550) * mm, "end": v(175, 1500) * mm});
            skLineSegment(sketch, "E52.bottom", {"start": v(100, 1850) * mm, "end": v(175, 1850) * mm});
            skLineSegment(sketch, "E52.top", {"start": v(100, 1800) * mm, "end": v(175, 1800) * mm});
            skLineSegment(sketch, "E52.left", {"start": v(100, 1850) * mm, "end": v(100, 1800) * mm});
            skLineSegment(sketch, "E52.right", {"start": v(175, 1850) * mm, "end": v(175, 1800) * mm});
            skLineSegment(sketch, "E53.bottom", {"start": v(100, 2150) * mm, "end": v(175, 2150) * mm});
            skLineSegment(sketch, "E53.top", {"start": v(100, 2100) * mm, "end": v(175, 2100) * mm});
            skLineSegment(sketch, "E53.left", {"start": v(100, 2150) * mm, "end": v(100, 2100) * mm});
            skLineSegment(sketch, "E53.right", {"start": v(175, 2150) * mm, "end": v(175, 2100) * mm});
            skLineSegment(sketch, "E54.bottom", {"start": v(100, 2510) * mm, "end": v(175, 2510) * mm});
            skLineSegment(sketch, "E54.top", {"start": v(100, 2460) * mm, "end": v(175, 2460) * mm});
            skLineSegment(sketch, "E54.left", {"start": v(100, 2510) * mm, "end": v(100, 2460) * mm});
            skLineSegment(sketch, "E54.right", {"start": v(175, 2510) * mm, "end": v(175, 2460) * mm});
            skLineSegment(sketch, "E55.bottom", {"start": v(100, 2450) * mm, "end": v(175, 2450) * mm});
            skLineSegment(sketch, "E55.top", {"start": v(100, 2400) * mm, "end": v(175, 2400) * mm});
            skLineSegment(sketch, "E55.left", {"start": v(100, 2450) * mm, "end": v(100, 2400) * mm});
            skLineSegment(sketch, "E55.right", {"start": v(175, 2450) * mm, "end": v(175, 2400) * mm});
            skSolve(sketch);
        }
        {
            var Q0;
            Q0 = qSketchRegion(id + "F46", true);
            var Q1;
            Q1=makeQuery(id+"F45.opExtrude","SWEPT_FACE",FACE,{"disambiguationData":[OSD([sQuery(id+"F44.wireOp",EDGE,"E42.left")])]});
            extrude(context, id + "F47", {"entities" : qUnion([Q0]), "endBound" : BoundingType.UP_TO_SURFACE, "endBoundEntityFace" : qUnion([Q1]), "depth" : 25 * mm});
        }
        {
            var Q0;
            Q0=makeQuery(id+"F43.opExtrude","SWEPT_FACE",FACE,{"disambiguationData":[OSD([sQuery(id+"F42.wireOp",EDGE,"E41.top")])]});
            var sketch = newSketch(context, id + "F48", { "sketchPlane" : qUnion([Q0])});
            skLineSegment(sketch, "E56.bottom", {"start": v(1500, 25) * mm, "end": v(510, 25) * mm});
            skLineSegment(sketch, "E56.top", {"start": v(1500, 625) * mm, "end": v(510, 625) * mm});
            skLineSegment(sketch, "E56.left", {"start": v(1500, 25) * mm, "end": v(1500, 625) * mm});
            skLineSegment(sketch, "E56.right", {"start": v(510, 25) * mm, "end": v(510, 625) * mm});
            skSolve(sketch);
        }
        {
            var Q0;
            Q0 = qSketchRegion(id + "F48", true);
            extrude(context, id + "F49", {"entities" : qUnion([Q0]), "depth" : 12 * mm});
        }
        {
            var Q0;
            Q0=makeQuery(id+"F49.opExtrude","SWEPT_BODY",BODY,{"disambiguationData":[OSD([sQuery(id+"F48.wireOp",EDGE,"E56.bottom"),sQuery(id+"F48.wireOp",EDGE,"E56.top"),sQuery(id+"F48.wireOp",EDGE,"E56.left"),sQuery(id+"F48.wireOp",EDGE,"E56.right")])]});
            transform(context, id + "F50", {"entities" : qUnion([Q0]), "transformType" : TransformType.TRANSLATION_3D, "dx" : 0 * mm, "dy" : 0 * mm, "dz" : 600 * mm, "makeCopy" : true});
        }
        {
            var Q0;
            Q0=makeQuery(id+"F50.opPattern","COPY",BODY,{"derivedFrom":makeQuery(id+"F49.opExtrude","SWEPT_BODY",BODY,{"disambiguationData":[OSD([sQuery(id+"F48.wireOp",EDGE,"E56.bottom"),sQuery(id+"F48.wireOp",EDGE,"E56.top"),sQuery(id+"F48.wireOp",EDGE,"E56.left"),sQuery(id+"F48.wireOp",EDGE,"E56.right")])]}),"instanceName":"1"});
            transform(context, id + "F51", {"entities" : qUnion([Q0]), "transformType" : TransformType.TRANSLATION_3D, "dx" : 0 * mm, "dy" : 0 * mm, "dz" : 600 * mm, "makeCopy" : true});
        }
        {
            var Q0;
            Q0=makeQuery(id+"F51.opPattern","COPY",BODY,{"derivedFrom":makeQuery(id+"F50.opPattern","COPY",BODY,{"derivedFrom":makeQuery(id+"F49.opExtrude","SWEPT_BODY",BODY,{"disambiguationData":[OSD([sQuery(id+"F48.wireOp",EDGE,"E56.bottom"),sQuery(id+"F48.wireOp",EDGE,"E56.top"),sQuery(id+"F48.wireOp",EDGE,"E56.left"),sQuery(id+"F48.wireOp",EDGE,"E56.right")])]}),"instanceName":"1"}),"instanceName":"1"});
            transform(context, id + "F52", {"entities" : qUnion([Q0]), "transformType" : TransformType.TRANSLATION_3D, "dx" : 0 * mm, "dy" : 0 * mm, "dz" : 600 * mm, "makeCopy" : true});
        }
        {
            var Q0;
            Q0=makeQuery(id+"F51.opPattern","COPY",FACE,{"derivedFrom":makeQuery(id+"F50.opPattern","COPY",FACE,{"derivedFrom":makeQuery(id+"F49.opExtrude","CAP_FACE",FACE,{"disambiguationData":[OSD([sQuery(id+"F48.wireOp",EDGE,"E56.bottom"),sQuery(id+"F48.wireOp",EDGE,"E56.top"),sQuery(id+"F48.wireOp",EDGE,"E56.left"),sQuery(id+"F48.wireOp",EDGE,"E56.right")])],"isStart":false}),"instanceName":"1"}),"instanceName":"1"});
            var sketch = newSketch(context, id + "F53", { "sketchPlane" : qUnion([Q0])});
            skLineSegment(sketch, "E57.bottom", {"start": v(925, 1800) * mm, "end": v(1175, 1800) * mm});
            skLineSegment(sketch, "E57.top", {"start": v(925, 1250) * mm, "end": v(1175, 1250) * mm});
            skLineSegment(sketch, "E57.left", {"start": v(925, 1800) * mm, "end": v(925, 1250) * mm});
            skLineSegment(sketch, "E57.right", {"start": v(1175, 1800) * mm, "end": v(1175, 1250) * mm});
            skSolve(sketch);
        }
        {
            var Q0;
            Q0 = qSketchRegion(id + "F53", true);
            extrude(context, id + "F54", {"entities" : qUnion([Q0]), "operationType" : NewBodyOperationType.REMOVE, "oppositeDirection" : true, "depth" : 106 * mm});
        }
        {
            var Q0;
            {var subQ0=sQuery(id+"F2.wireOp",EDGE,"E6.right");var subQ1=sQuery(id+"F2.wireOp",EDGE,"E6.bottom");var subQ2=makeQuery(id+"F3.opExtrude","CAP_FACE",FACE,{"disambiguationData":[OSD([subQ1,sQuery(id+"F2.wireOp",EDGE,"E6.top"),sQuery(id+"F2.wireOp",EDGE,"E6.left"),subQ0])],"isStart":false});Q0=makeQuery(id+"F5.boolean.opBoolean","MERGE",FACE,{"derivedFrom":[makeQuery(id+"F3.boolean.opBoolean","SPLIT",FACE,{"disambiguationData":[TD([makeQuery(id+"F1.opExtrude","SWEPT_FACE",FACE,{"disambiguationData":[OSD([sQuery(id+"F0.wireOp",EDGE,"E5.2")])]})])],"derivedFrom":subQ2}),makeQuery(id+"F3.boolean.opBoolean","SPLIT",FACE,{"disambiguationData":[TD([makeQuery(id+"F1.opExtrude","SWEPT_FACE",FACE,{"disambiguationData":[OSD([sQuery(id+"F0.wireOp",EDGE,"E0.bottom")])]})])],"derivedFrom":subQ2}),makeQuery(id+"F5.opExtrude","SWEPT_FACE",FACE,{"disambiguationData":[OSD([sQuery(id+"F4.wireOp",EDGE,"E7.bottom")])]})]});}
            var sketch = newSketch(context, id + "F55", { "sketchPlane" : qUnion([Q0])});
            skLineSegment(sketch, "E58.bottom", {"start": v(-1410, 1403) * mm, "end": v(-510, 1403) * mm});
            skLineSegment(sketch, "E58.top", {"start": v(-1410, 197) * mm, "end": v(-510, 197) * mm});
            skLineSegment(sketch, "E58.left", {"start": v(-1410, 1403) * mm, "end": v(-1410, 197) * mm});
            skLineSegment(sketch, "E58.right", {"start": v(-510, 1403) * mm, "end": v(-510, 197) * mm});
            skSolve(sketch);
        }
        {
            var Q0;
            Q0 = qSketchRegion(id + "F55", true);
            extrude(context, id + "F56", {"entities" : qUnion([Q0]), "depth" : 22 * mm});
        }
        {
            var Q0;
            Q0=makeQuery(id+"F47.opExtrude","SWEPT_FACE",FACE,{"disambiguationData":[OSD([sQuery(id+"F46.wireOp",EDGE,"E52.top")])]});
            var sketch = newSketch(context, id + "F57", { "sketchPlane" : qUnion([Q0])});
            skLineSegment(sketch, "E59.bottom", {"start": v(-925, -100) * mm, "end": v(-1175, -100) * mm});
            skLineSegment(sketch, "E59.top", {"start": v(-925, -140) * mm, "end": v(-1175, -140) * mm});
            skLineSegment(sketch, "E59.left", {"start": v(-925, -100) * mm, "end": v(-925, -140) * mm});
            skLineSegment(sketch, "E59.right", {"start": v(-1175, -100) * mm, "end": v(-1175, -140) * mm});
            skSolve(sketch);
        }
        {
            var Q0;
            Q0 = qSketchRegion(id + "F57", true);
            extrude(context, id + "F58", {"entities" : qUnion([Q0]), "operationType" : NewBodyOperationType.REMOVE, "oppositeDirection" : true, "depth" : 25 * mm});
        }
        {
            var Q0;
            Q0=makeQuery(id+"F51.opPattern","COPY",FACE,{"derivedFrom":makeQuery(id+"F50.opPattern","COPY",FACE,{"derivedFrom":makeQuery(id+"F49.opExtrude","CAP_FACE",FACE,{"disambiguationData":[OSD([sQuery(id+"F48.wireOp",EDGE,"E56.bottom"),sQuery(id+"F48.wireOp",EDGE,"E56.top"),sQuery(id+"F48.wireOp",EDGE,"E56.left"),sQuery(id+"F48.wireOp",EDGE,"E56.right")])],"isStart":false}),"instanceName":"1"}),"instanceName":"1"});
            var sketch = newSketch(context, id + "F59", { "sketchPlane" : qUnion([Q0])});
            skLineSegment(sketch, "E60.bottom", {"start": v(510, 1569.36) * mm, "end": v(710, 1569.36) * mm});
            skLineSegment(sketch, "E60.top", {"start": v(510, 1469.36) * mm, "end": v(710, 1469.36) * mm});
            skLineSegment(sketch, "E60.left", {"start": v(510, 1569.36) * mm, "end": v(510, 1469.36) * mm});
            skLineSegment(sketch, "E60.right", {"start": v(710, 1569.36) * mm, "end": v(710, 1469.36) * mm});
            skLineSegment(sketch, "E61.bottom", {"start": v(713, 1569.36) * mm, "end": v(913, 1569.36) * mm});
            skLineSegment(sketch, "E61.top", {"start": v(713, 1469.36) * mm, "end": v(913, 1469.36) * mm});
            skLineSegment(sketch, "E61.left", {"start": v(713, 1569.36) * mm, "end": v(713, 1469.36) * mm});
            skLineSegment(sketch, "E61.right", {"start": v(913, 1569.36) * mm, "end": v(913, 1469.36) * mm});
            skLineSegment(sketch, "E62.bottom", {"start": v(1186.03, 1569.36) * mm, "end": v(1386.03, 1569.36) * mm});
            skLineSegment(sketch, "E62.top", {"start": v(1186.03, 1469.36) * mm, "end": v(1386.03, 1469.36) * mm});
            skLineSegment(sketch, "E62.left", {"start": v(1186.03, 1569.36) * mm, "end": v(1186.03, 1469.36) * mm});
            skLineSegment(sketch, "E62.right", {"start": v(1386.03, 1569.36) * mm, "end": v(1386.03, 1469.36) * mm});
            skLineSegment(sketch, "E63.bottom", {"start": v(1421.48, 1569.36) * mm, "end": v(1475.72, 1569.36) * mm});
            skLineSegment(sketch, "E63.top", {"start": v(1421.48, 1469.36) * mm, "end": v(1475.72, 1469.36) * mm});
            skLineSegment(sketch, "E63.left", {"start": v(1421.48, 1569.36) * mm, "end": v(1421.48, 1469.36) * mm});
            skLineSegment(sketch, "E63.right", {"start": v(1475.72, 1569.36) * mm, "end": v(1475.72, 1469.36) * mm});
            skSolve(sketch);
        }
        {
            var Q0;
            Q0=makeQuery(id+"F3.boolean.opBoolean","MERGE",FACE,{"derivedFrom":[makeQuery(id+"F1.opExtrude","CAP_FACE",FACE,{"disambiguationData":[OSD([sQuery(id+"F0.wireOp",EDGE,"E0.bottom"),sQuery(id+"F0.wireOp",EDGE,"E0.top"),sQuery(id+"F0.wireOp",EDGE,"E0.left"),sQuery(id+"F0.wireOp",EDGE,"E0.right"),sQuery(id+"F0.wireOp",EDGE,"E1"),sQuery(id+"F0.wireOp",EDGE,"E2"),sQuery(id+"F0.wireOp",EDGE,"E3"),sQuery(id+"F0.wireOp",EDGE,"E4"),sQuery(id+"F0.wireOp",EDGE,"E5.0"),sQuery(id+"F0.wireOp",EDGE,"E5.1"),sQuery(id+"F0.wireOp",EDGE,"E5.2"),sQuery(id+"F0.wireOp",EDGE,"E5.3"),sQuery(id+"F0.wireOp",EDGE,"E5.4"),sQuery(id+"F0.wireOp",EDGE,"E5.5"),sQuery(id+"F0.wireOp",EDGE,"E5.6"),sQuery(id+"F0.wireOp",EDGE,"E5.7")])],"isStart":true}),makeQuery(id+"F3.opExtrude","CAP_FACE",FACE,{"disambiguationData":[OSD([sQuery(id+"F2.wireOp",EDGE,"E6.bottom"),sQuery(id+"F2.wireOp",EDGE,"E6.top"),sQuery(id+"F2.wireOp",EDGE,"E6.left"),sQuery(id+"F2.wireOp",EDGE,"E6.right")])],"isStart":true})]});
            var sketch = newSketch(context, id + "F60", { "sketchPlane" : qUnion([Q0])});
            skLineSegment(sketch, "E64.bottom", {"start": v(-1162.5, 1650) * mm, "end": v(-1237.5, 1650) * mm});
            skLineSegment(sketch, "E64.top", {"start": v(-1162.5, -1650) * mm, "end": v(-1237.5, -1650) * mm});
            skLineSegment(sketch, "E64.left", {"start": v(-1237.5, 1650) * mm, "end": v(-1237.5, -1650) * mm});
            skLineSegment(sketch, "E64.right", {"start": v(-1162.5, 1650) * mm, "end": v(-1162.5, -1650) * mm});
            skLineSegment(sketch, "E65.bottom", {"start": v(-687.5, 1650) * mm, "end": v(-762.5, 1650) * mm});
            skLineSegment(sketch, "E65.top", {"start": v(-687.5, -1650) * mm, "end": v(-762.5, -1650) * mm});
            skLineSegment(sketch, "E65.left", {"start": v(-687.5, 1650) * mm, "end": v(-687.5, -1650) * mm});
            skLineSegment(sketch, "E65.right", {"start": v(-762.5, 1650) * mm, "end": v(-762.5, -1650) * mm});
            skLineSegment(sketch, "E66.bottom", {"start": v(-287.5, 1650) * mm, "end": v(-362.5, 1650) * mm});
            skLineSegment(sketch, "E66.top", {"start": v(-287.5, -1650) * mm, "end": v(-362.5, -1650) * mm});
            skLineSegment(sketch, "E66.left", {"start": v(-287.5, 1650) * mm, "end": v(-287.5, -1650) * mm});
            skLineSegment(sketch, "E66.right", {"start": v(-362.5, 1650) * mm, "end": v(-362.5, -1650) * mm});
            skLineSegment(sketch, "E67.bottom", {"start": v(437.5, 1650) * mm, "end": v(362.5, 1650) * mm});
            skLineSegment(sketch, "E67.top", {"start": v(437.5, -1650) * mm, "end": v(362.5, -1650) * mm});
            skLineSegment(sketch, "E67.left", {"start": v(437.5, 1650) * mm, "end": v(437.5, -1650) * mm});
            skLineSegment(sketch, "E67.right", {"start": v(362.5, 1650) * mm, "end": v(362.5, -1650) * mm});
            skLineSegment(sketch, "E68.bottom", {"start": v(37.5, 1650) * mm, "end": v(-37.5, 1650) * mm});
            skLineSegment(sketch, "E68.top", {"start": v(37.5, -1650) * mm, "end": v(-37.5, -1650) * mm});
            skLineSegment(sketch, "E68.left", {"start": v(-37.5, 1650) * mm, "end": v(-37.5, -1650) * mm});
            skLineSegment(sketch, "E68.right", {"start": v(37.5, 1650) * mm, "end": v(37.5, -1650) * mm});
            skLineSegment(sketch, "E69.bottom", {"start": v(837.5, 1650) * mm, "end": v(762.5, 1650) * mm});
            skLineSegment(sketch, "E69.top", {"start": v(837.5, -1650) * mm, "end": v(762.5, -1650) * mm});
            skLineSegment(sketch, "E69.left", {"start": v(837.5, 1650) * mm, "end": v(837.5, -1650) * mm});
            skLineSegment(sketch, "E69.right", {"start": v(762.5, 1650) * mm, "end": v(762.5, -1650) * mm});
            skLineSegment(sketch, "E70.bottom", {"start": v(1237.5, 1650) * mm, "end": v(1162.5, 1650) * mm});
            skLineSegment(sketch, "E70.top", {"start": v(1237.5, -1650) * mm, "end": v(1162.5, -1650) * mm});
            skLineSegment(sketch, "E70.left", {"start": v(1237.5, 1650) * mm, "end": v(1237.5, -1650) * mm});
            skLineSegment(sketch, "E70.right", {"start": v(1162.5, 1650) * mm, "end": v(1162.5, -1650) * mm});
            skLineSegment(sketch, "E71.bottom", {"start": v(1637.5, 1650) * mm, "end": v(1562.5, 1650) * mm});
            skLineSegment(sketch, "E71.top", {"start": v(1637.5, -1650) * mm, "end": v(1562.5, -1650) * mm});
            skLineSegment(sketch, "E71.left", {"start": v(1637.5, 1650) * mm, "end": v(1637.5, -1650) * mm});
            skLineSegment(sketch, "E71.right", {"start": v(1562.5, 1650) * mm, "end": v(1562.5, -1650) * mm});
            skLineSegment(sketch, "E72.bottom", {"start": v(-1537.5, -1650) * mm, "end": v(-1462.5, -1650) * mm});
            skLineSegment(sketch, "E72.top", {"start": v(-1537.5, 1650) * mm, "end": v(-1462.5, 1650) * mm});
            skLineSegment(sketch, "E72.left", {"start": v(-1537.5, -1650) * mm, "end": v(-1537.5, 1650) * mm});
            skLineSegment(sketch, "E72.right", {"start": v(-1462.5, -1650) * mm, "end": v(-1462.5, 1650) * mm});
            skSolve(sketch);
        }
        {
            var Q0;
            Q0 = qSketchRegion(id + "F60", true);
            extrude(context, id + "F61", {"entities" : qUnion([Q0]), "depth" : 210 * mm});
        }
        {
            var Q0;
            {var subQ0=sQuery(id+"F2.wireOp",EDGE,"E6.right");var subQ1=sQuery(id+"F2.wireOp",EDGE,"E6.bottom");var subQ2=makeQuery(id+"F3.opExtrude","CAP_FACE",FACE,{"disambiguationData":[OSD([subQ1,sQuery(id+"F2.wireOp",EDGE,"E6.top"),sQuery(id+"F2.wireOp",EDGE,"E6.left"),subQ0])],"isStart":false});Q0=makeQuery(id+"F5.boolean.opBoolean","MERGE",FACE,{"derivedFrom":[makeQuery(id+"F3.boolean.opBoolean","SPLIT",FACE,{"disambiguationData":[TD([makeQuery(id+"F1.opExtrude","SWEPT_FACE",FACE,{"disambiguationData":[OSD([sQuery(id+"F0.wireOp",EDGE,"E5.2")])]})])],"derivedFrom":subQ2}),makeQuery(id+"F3.boolean.opBoolean","SPLIT",FACE,{"disambiguationData":[TD([makeQuery(id+"F1.opExtrude","SWEPT_FACE",FACE,{"disambiguationData":[OSD([sQuery(id+"F0.wireOp",EDGE,"E0.bottom")])]})])],"derivedFrom":subQ2}),makeQuery(id+"F5.opExtrude","SWEPT_FACE",FACE,{"disambiguationData":[OSD([sQuery(id+"F4.wireOp",EDGE,"E7.bottom")])]})]});}
            var sketch = newSketch(context, id + "F62", { "sketchPlane" : qUnion([Q0])});
            skLineSegment(sketch, "E73.bottom", {"start": v(-1500, 1413) * mm, "end": v(-476.93, 1413) * mm});
            skLineSegment(sketch, "E73.top", {"start": v(-1500, 187) * mm, "end": v(-476.93, 187) * mm});
            skLineSegment(sketch, "E73.left", {"start": v(-1500, 1413) * mm, "end": v(-1500, 187) * mm});
            skLineSegment(sketch, "E73.right", {"start": v(-476.93, 1413) * mm, "end": v(-476.93, 187) * mm});
            skSolve(sketch);
        }
        {
            var Q0;
            Q0 = qSketchRegion(id + "F62", true);
            extrude(context, id + "F63", {"entities" : qUnion([Q0]), "operationType" : NewBodyOperationType.REMOVE, "oppositeDirection" : true, "depth" : 25 * mm});
        }
        {
            var Q0;
            Q0=makeQuery(id+"F56.opExtrude","CAP_FACE",FACE,{"disambiguationData":[OSD([sQuery(id+"F55.wireOp",EDGE,"E58.bottom"),sQuery(id+"F55.wireOp",EDGE,"E58.top"),sQuery(id+"F55.wireOp",EDGE,"E58.left"),sQuery(id+"F55.wireOp",EDGE,"E58.right")])],"isStart":false});
            var sketch = newSketch(context, id + "F64", { "sketchPlane" : qUnion([Q0])});
            skCircle(sketch, "E74", {"center": v(-960, 800) * mm, "radius": 175.9 * mm});
            skLineSegment(sketch, "E75", {"start": v(-1410, 1403) * mm, "end": v(-510, 197) * mm});
            skLineSegment(sketch, "E76", {"start": v(-1410, 197) * mm, "end": v(-510, 1403) * mm});
            skSolve(sketch);
        }
        {
            var Q0;
            Q0 = qSketchRegion(id + "F64", true);
            extrude(context, id + "F65", {"entities" : qUnion([Q0]), "operationType" : NewBodyOperationType.REMOVE, "oppositeDirection" : true, "depth" : 22 * mm});
        }
        {
            var Q0;
            Q0=makeQuery(id+"F56.opExtrude","CAP_FACE",FACE,{"disambiguationData":[OSD([sQuery(id+"F55.wireOp",EDGE,"E58.bottom"),sQuery(id+"F55.wireOp",EDGE,"E58.top"),sQuery(id+"F55.wireOp",EDGE,"E58.left"),sQuery(id+"F55.wireOp",EDGE,"E58.right")])],"isStart":false});
            var sketch = newSketch(context, id + "F66", { "sketchPlane" : qUnion([Q0])});
            skCircle(sketch, "E77", {"center": v(-960, 800) * mm, "radius": 174.9 * mm});
            skSolve(sketch);
        }
        {
            var Q0;
            Q0 = qSketchRegion(id + "F66", true);
            extrude(context, id + "F67", {"entities" : qUnion([Q0]), "oppositeDirection" : true, "depth" : 50 * mm});
        }
        {
            var Q0;
            Q0=makeQuery(id+"F67.opExtrude","CAP_FACE",FACE,{"disambiguationData":[OSD([sQuery(id+"F66.wireOp",EDGE,"E77")])],"isStart":false});
            var sketch = newSketch(context, id + "F68", { "sketchPlane" : qUnion([Q0])});
            skCircle(sketch, "E78", {"center": v(-960, -800) * mm, "radius": 58 * mm});
            skSolve(sketch);
        }
        {
            var Q0;
            Q0 = qSketchRegion(id + "F68", true);
            extrude(context, id + "F69", {"entities" : qUnion([Q0]), "operationType" : NewBodyOperationType.ADD, "depth" : 103 * mm});
        }
        {
            var Q0;
            Q0=makeQuery(id+"F61.opExtrude","SWEPT_FACE",FACE,{"disambiguationData":[OSD([sQuery(id+"F60.wireOp",EDGE,"E66.right")])]});
            var sketch = newSketch(context, id + "F70", { "sketchPlane" : qUnion([Q0])});
            skLineSegment(sketch, "E79.bottom", {"start": v(-162, 0) * mm, "end": v(-212, 0) * mm});
            skLineSegment(sketch, "E79.top", {"start": v(-162, -100) * mm, "end": v(-212, -100) * mm});
            skLineSegment(sketch, "E79.left", {"start": v(-162, 0) * mm, "end": v(-162, -100) * mm});
            skLineSegment(sketch, "E79.right", {"start": v(-212, 0) * mm, "end": v(-212, -100) * mm});
            skLineSegment(sketch, "E80.bottom", {"start": v(-1438, 0) * mm, "end": v(-1388, 0) * mm});
            skLineSegment(sketch, "E80.top", {"start": v(-1438, -100) * mm, "end": v(-1388, -100) * mm});
            skLineSegment(sketch, "E80.left", {"start": v(-1438, 0) * mm, "end": v(-1438, -100) * mm});
            skLineSegment(sketch, "E80.right", {"start": v(-1388, 0) * mm, "end": v(-1388, -100) * mm});
            skSolve(sketch);
        }
        {
            var Q0;
            Q0 = qSketchRegion(id + "F70", true);
            var Q1;
            Q1=makeQuery(id+"F61.opExtrude","SWEPT_FACE",FACE,{"disambiguationData":[OSD([sQuery(id+"F60.wireOp",EDGE,"E72.right")])]});
            extrude(context, id + "F71", {"entities" : qUnion([Q0]), "endBound" : BoundingType.UP_TO_SURFACE, "endBoundEntityFace" : qUnion([Q1]), "depth" : 25 * mm});
        }
        {
            var Q0;
            Q0=makeQuery(id+"F71.opExtrude","SWEPT_FACE",FACE,{"disambiguationData":[OSD([sQuery(id+"F70.wireOp",EDGE,"E79.right")])]});
            var sketch = newSketch(context, id + "F72", { "sketchPlane" : qUnion([Q0])});
            skLineSegment(sketch, "E81.bottom", {"start": v(485, 0) * mm, "end": v(535, 0) * mm});
            skLineSegment(sketch, "E81.top", {"start": v(485, -100) * mm, "end": v(535, -100) * mm});
            skLineSegment(sketch, "E81.left", {"start": v(485, 0) * mm, "end": v(485, -100) * mm});
            skLineSegment(sketch, "E81.right", {"start": v(535, 0) * mm, "end": v(535, -100) * mm});
            skLineSegment(sketch, "E82.bottom", {"start": v(1385, 0) * mm, "end": v(1435, 0) * mm});
            skLineSegment(sketch, "E82.top", {"start": v(1385, -100) * mm, "end": v(1435, -100) * mm});
            skLineSegment(sketch, "E82.left", {"start": v(1385, 0) * mm, "end": v(1385, -100) * mm});
            skLineSegment(sketch, "E82.right", {"start": v(1435, 0) * mm, "end": v(1435, -100) * mm});
            skSolve(sketch);
        }
        {
            var Q0;
            Q0 = qSketchRegion(id + "F72", true);
            extrude(context, id + "F73", {"entities" : qUnion([Q0]), "endBound" : BoundingType.UP_TO_NEXT, "depth" : 25 * mm});
        }
        {
            var Q0;
            {var subQ0=sQuery(id+"F2.wireOp",EDGE,"E6.right");var subQ1=sQuery(id+"F2.wireOp",EDGE,"E6.bottom");var subQ2=makeQuery(id+"F3.opExtrude","CAP_FACE",FACE,{"disambiguationData":[OSD([subQ1,sQuery(id+"F2.wireOp",EDGE,"E6.top"),sQuery(id+"F2.wireOp",EDGE,"E6.left"),subQ0])],"isStart":false});Q0=makeQuery(id+"F5.boolean.opBoolean","MERGE",FACE,{"derivedFrom":[makeQuery(id+"F3.boolean.opBoolean","SPLIT",FACE,{"disambiguationData":[TD([makeQuery(id+"F1.opExtrude","SWEPT_FACE",FACE,{"disambiguationData":[OSD([sQuery(id+"F0.wireOp",EDGE,"E5.2")])]})])],"derivedFrom":subQ2}),makeQuery(id+"F3.boolean.opBoolean","SPLIT",FACE,{"disambiguationData":[TD([makeQuery(id+"F1.opExtrude","SWEPT_FACE",FACE,{"disambiguationData":[OSD([sQuery(id+"F0.wireOp",EDGE,"E0.bottom")])]})])],"derivedFrom":subQ2}),makeQuery(id+"F5.opExtrude","SWEPT_FACE",FACE,{"disambiguationData":[OSD([sQuery(id+"F4.wireOp",EDGE,"E7.bottom")])]})]});}
            var sketch = newSketch(context, id + "F74", { "sketchPlane" : qUnion([Q0])});
            skLineSegment(sketch, "E83.bottom", {"start": v(-510, -1500) * mm, "end": v(1648.33, -1500) * mm});
            skLineSegment(sketch, "E83.top", {"start": v(-510, 1661.1) * mm, "end": v(1648.33, 1661.1) * mm});
            skLineSegment(sketch, "E83.left", {"start": v(-510, -1500) * mm, "end": v(-510, 1661.1) * mm});
            skLineSegment(sketch, "E83.right", {"start": v(1648.33, -1500) * mm, "end": v(1648.33, 1661.1) * mm});
            skSolve(sketch);
        }
        {
            var Q0;
            Q0 = qSketchRegion(id + "F74", true);
            extrude(context, id + "F75", {"entities" : qUnion([Q0]), "operationType" : NewBodyOperationType.REMOVE, "oppositeDirection" : true, "depth" : 25 * mm});
        }
        {
            var Q0;
            Q0=makeQuery(id+"F16.opPattern","COPY",BODY,{"derivedFrom":makeQuery(id+"F15.opExtrude","SWEPT_BODY",BODY,{"disambiguationData":[OSD([sQuery(id+"F14.wireOp",EDGE,"E30.bottom"),sQuery(id+"F14.wireOp",EDGE,"E30.top"),sQuery(id+"F14.wireOp",EDGE,"E30.left"),sQuery(id+"F14.wireOp",EDGE,"E30.right")])]}),"instanceName":"1"});
            deleteBodies(context, id + "F76", {"entities" : qUnion([Q0])});
        }
        {
            var Q0;
            {var subQ0=sQuery(id+"F2.wireOp",EDGE,"E6.right");var subQ1=sQuery(id+"F2.wireOp",EDGE,"E6.bottom");var subQ2=makeQuery(id+"F3.opExtrude","CAP_FACE",FACE,{"disambiguationData":[OSD([subQ1,sQuery(id+"F2.wireOp",EDGE,"E6.top"),sQuery(id+"F2.wireOp",EDGE,"E6.left"),subQ0])],"isStart":false});Q0=makeQuery(id+"F5.boolean.opBoolean","MERGE",FACE,{"derivedFrom":[makeQuery(id+"F3.boolean.opBoolean","SPLIT",FACE,{"disambiguationData":[TD([makeQuery(id+"F1.opExtrude","SWEPT_FACE",FACE,{"disambiguationData":[OSD([sQuery(id+"F0.wireOp",EDGE,"E5.2")])]})])],"derivedFrom":subQ2}),makeQuery(id+"F3.boolean.opBoolean","SPLIT",FACE,{"disambiguationData":[TD([makeQuery(id+"F1.opExtrude","SWEPT_FACE",FACE,{"disambiguationData":[OSD([sQuery(id+"F0.wireOp",EDGE,"E0.bottom")])]})])],"derivedFrom":subQ2}),makeQuery(id+"F5.opExtrude","SWEPT_FACE",FACE,{"disambiguationData":[OSD([sQuery(id+"F4.wireOp",EDGE,"E7.bottom")])]})]});}
            var sketch = newSketch(context, id + "F77", { "sketchPlane" : qUnion([Q0])});
            skLineSegment(sketch, "E84.bottom", {"start": v(-476.93, 1413) * mm, "end": v(1647.25, 1413) * mm});
            skLineSegment(sketch, "E84.top", {"start": v(-476.93, -1644.5) * mm, "end": v(1647.25, -1644.5) * mm});
            skLineSegment(sketch, "E84.left", {"start": v(-476.93, 1413) * mm, "end": v(-476.93, -1644.5) * mm});
            skLineSegment(sketch, "E84.right", {"start": v(1647.25, 1413) * mm, "end": v(1647.25, -1644.5) * mm});
            skSolve(sketch);
        }
        {
            var Q0;
            Q0 = qSketchRegion(id + "F77", true);
            extrude(context, id + "F78", {"entities" : qUnion([Q0]), "operationType" : NewBodyOperationType.REMOVE, "oppositeDirection" : true, "depth" : 25 * mm});
        }
        {
            var Q0;
            Q0=makeQuery(id+"F1.opExtrude","SWEPT_FACE",FACE,{"disambiguationData":[OSD([sQuery(id+"F0.wireOp",EDGE,"E0.left")])]});
            var sketch = newSketch(context, id + "F79", { "sketchPlane" : qUnion([Q0])});
            skLineSegment(sketch, "E85.bottom", {"start": v(-1331.1, 925) * mm, "end": v(-131.1, 925) * mm});
            skLineSegment(sketch, "E85.top", {"start": v(-1331.1, 25) * mm, "end": v(-131.1, 25) * mm});
            skLineSegment(sketch, "E85.left", {"start": v(-1331.1, 925) * mm, "end": v(-1331.1, 25) * mm});
            skLineSegment(sketch, "E85.right", {"start": v(-131.1, 925) * mm, "end": v(-131.1, 25) * mm});
            skLineSegment(sketch, "E86.bottom", {"start": v(-131.1, 925) * mm, "end": v(468.9, 925) * mm});
            skLineSegment(sketch, "E86.top", {"start": v(-131.1, 25) * mm, "end": v(468.9, 25) * mm});
            skLineSegment(sketch, "E86.right", {"start": v(468.9, 925) * mm, "end": v(468.9, 25) * mm});
            skSolve(sketch);
        }
        {
            var Q0;
            Q0 = qSketchRegion(id + "F79", true);
            extrude(context, id + "F80", {"entities" : qUnion([Q0]), "depth" : 12.5 * mm});
        }
        {
            var Q0;
            Q0=makeQuery(id+"F61.opExtrude","CAP_FACE",FACE,{"disambiguationData":[OSD([sQuery(id+"F60.wireOp",EDGE,"E66.bottom"),sQuery(id+"F60.wireOp",EDGE,"E66.top"),sQuery(id+"F60.wireOp",EDGE,"E66.left"),sQuery(id+"F60.wireOp",EDGE,"E66.right")])],"isStart":true});
            var sketch = newSketch(context, id + "F81", { "sketchPlane" : qUnion([Q0])});
            skLineSegment(sketch, "E87.bottom", {"start": v(-362.5, 1391.15) * mm, "end": v(837.5, 1391.15) * mm});
            skLineSegment(sketch, "E87.top", {"start": v(-362.5, -1008.85) * mm, "end": v(837.5, -1008.85) * mm});
            skLineSegment(sketch, "E87.left", {"start": v(-362.5, 1391.15) * mm, "end": v(-362.5, -1008.85) * mm});
            skLineSegment(sketch, "E87.right", {"start": v(837.5, 1391.15) * mm, "end": v(837.5, -1008.85) * mm});
            skSolve(sketch);
        }
        {
            var Q0;
            Q0 = qSketchRegion(id + "F81", true);
            extrude(context, id + "F82", {"entities" : qUnion([Q0]), "depth" : 22 * mm});
        }
        {
            var Q0;
            Q0=makeQuery(id+"F82.opExtrude","CAP_FACE",FACE,{"disambiguationData":[OSD([sQuery(id+"F81.wireOp",EDGE,"E87.bottom"),sQuery(id+"F81.wireOp",EDGE,"E87.top"),sQuery(id+"F81.wireOp",EDGE,"E87.left"),sQuery(id+"F81.wireOp",EDGE,"E87.right")])],"isStart":false});
            var sketch = newSketch(context, id + "F83", { "sketchPlane" : qUnion([Q0])});
            skLineSegment(sketch, "E88.bottom", {"start": v(737.5, 1331.1) * mm, "end": v(1487.5, 1331.1) * mm});
            skLineSegment(sketch, "E88.top", {"start": v(737.5, -468.9) * mm, "end": v(1487.5, -468.9) * mm});
            skLineSegment(sketch, "E88.left", {"start": v(737.5, 1331.1) * mm, "end": v(737.5, -468.9) * mm});
            skLineSegment(sketch, "E88.right", {"start": v(1487.5, 1331.1) * mm, "end": v(1487.5, -468.9) * mm});
            skSolve(sketch);
        }
        {
            var Q0;
            Q0 = qSketchRegion(id + "F83", true);
            extrude(context, id + "F84", {"entities" : qUnion([Q0]), "depth" : 700 * mm});
        }
        {
            var Q0;
            Q0=makeQuery(id+"F84.opExtrude","CAP_FACE",FACE,{"disambiguationData":[OSD([sQuery(id+"F83.wireOp",EDGE,"E88.bottom"),sQuery(id+"F83.wireOp",EDGE,"E88.top"),sQuery(id+"F83.wireOp",EDGE,"E88.left"),sQuery(id+"F83.wireOp",EDGE,"E88.right")])],"isStart":false});
            var sketch = newSketch(context, id + "F85", { "sketchPlane" : qUnion([Q0])});
            skLineSegment(sketch, "E89.0", {"start": v(1407.5, 1251.1) * mm, "end": v(817.5, 1251.1) * mm});
            skLineSegment(sketch, "E89.1", {"start": v(1407.5, -388.9) * mm, "end": v(1407.5, 1251.1) * mm});
            skLineSegment(sketch, "E89.2", {"start": v(817.5, -388.9) * mm, "end": v(1407.5, -388.9) * mm});
            skLineSegment(sketch, "E89.3", {"start": v(817.5, 1251.1) * mm, "end": v(817.5, -388.9) * mm});
            skSolve(sketch);
        }
        {
            var Q0;
            Q0 = qSketchRegion(id + "F85", true);
            extrude(context, id + "F86", {"entities" : qUnion([Q0]), "operationType" : NewBodyOperationType.REMOVE, "oppositeDirection" : true, "depth" : 500 * mm});
        }
        {
            var Q0;
            Q0=makeQuery(id+"F1.opExtrude","CAP_FACE",FACE,{"disambiguationData":[OSD([sQuery(id+"F0.wireOp",EDGE,"E0.bottom"),sQuery(id+"F0.wireOp",EDGE,"E0.top"),sQuery(id+"F0.wireOp",EDGE,"E0.left"),sQuery(id+"F0.wireOp",EDGE,"E0.right"),sQuery(id+"F0.wireOp",EDGE,"E1"),sQuery(id+"F0.wireOp",EDGE,"E2"),sQuery(id+"F0.wireOp",EDGE,"E3"),sQuery(id+"F0.wireOp",EDGE,"E4"),sQuery(id+"F0.wireOp",EDGE,"E5.0"),sQuery(id+"F0.wireOp",EDGE,"E5.1"),sQuery(id+"F0.wireOp",EDGE,"E5.2"),sQuery(id+"F0.wireOp",EDGE,"E5.3"),sQuery(id+"F0.wireOp",EDGE,"E5.4"),sQuery(id+"F0.wireOp",EDGE,"E5.5"),sQuery(id+"F0.wireOp",EDGE,"E5.6"),sQuery(id+"F0.wireOp",EDGE,"E5.7")])],"isStart":false});
            var sketch = newSketch(context, id + "F87", { "sketchPlane" : qUnion([Q0])});
            skLineSegment(sketch, "E90.bottom", {"start": v(1650, -1650) * mm, "end": v(-1650, -1650) * mm});
            skLineSegment(sketch, "E90.top", {"start": v(1650, 1650) * mm, "end": v(-1650, 1650) * mm});
            skLineSegment(sketch, "E90.left", {"start": v(1650, -1650) * mm, "end": v(1650, 1650) * mm});
            skLineSegment(sketch, "E90.right", {"start": v(-1650, -1650) * mm, "end": v(-1650, 1650) * mm});
            skSolve(sketch);
        }
        {
            var Q0;
            Q0 = qSketchRegion(id + "F87", true);
            extrude(context, id + "F88", {"entities" : qUnion([Q0]), "depth" : 25 * mm});
        }
        {
            var Q0;
            Q0=makeQuery(id+"F88.opExtrude","CAP_FACE",FACE,{"disambiguationData":[OSD([sQuery(id+"F87.wireOp",EDGE,"E90.bottom"),sQuery(id+"F87.wireOp",EDGE,"E90.top"),sQuery(id+"F87.wireOp",EDGE,"E90.left"),sQuery(id+"F87.wireOp",EDGE,"E90.right")])],"isStart":true});
            var sketch = newSketch(context, id + "F89", { "sketchPlane" : qUnion([Q0])});
            skCircle(sketch, "E91", {"center": v(-1005, -800) * mm, "radius": 10 * mm});
            skCircle(sketch, "E92", {"center": v(-1005, -300) * mm, "radius": 37.5 * mm});
            skCircle(sketch, "E93", {"center": v(-1005, -1300) * mm, "radius": 37.5 * mm});
            skLineSegment(sketch, "E94", {"start": v(-1500, -1413) * mm, "end": v(-510, -187) * mm});
            skLineSegment(sketch, "E95", {"start": v(-1500, -187) * mm, "end": v(-510, -1413) * mm});
            skCircle(sketch, "E96", {"center": v(-1405, -800) * mm, "radius": 50 * mm});
            skSolve(sketch);
        }
        {
            var Q0;
            Q0 = qSketchRegion(id + "F89", true);
            extrude(context, id + "F90", {"entities" : qUnion([Q0]), "operationType" : NewBodyOperationType.REMOVE, "oppositeDirection" : true, "depth" : 25 * mm});
        }
    });
